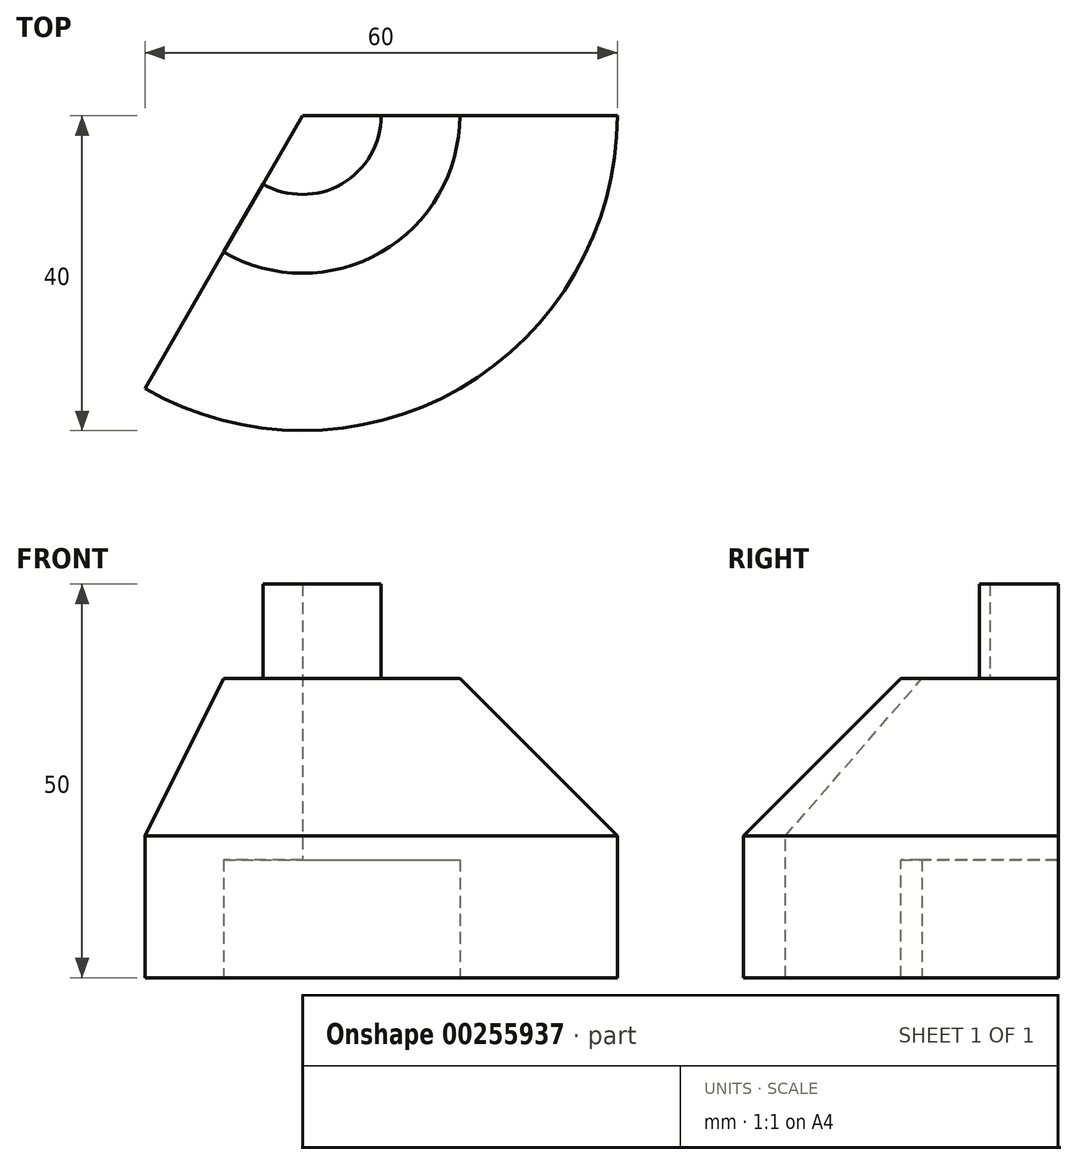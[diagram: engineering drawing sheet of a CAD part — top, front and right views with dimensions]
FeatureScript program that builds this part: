
annotation { "Feature Type Name" : "Feature", "Feature Type Description" : "" }
export const myFeature = defineFeature(function(context is Context, id is Id, definition is map)
    precondition{}
    {
        {
            var Q0;
            Q0=qCreatedBy(makeId("Front.planeOp"),FACE);
            var sketch = newSketch(context, id + "F0", { "sketchPlane" : qUnion([Q0])});
            skLineSegment(sketch, "E0", {"start": v(15.92, 20.7) * mm, "end": v(15.92, -14.3) * mm});
            skLineSegment(sketch, "E1", {"start": v(15.92, -14.3) * mm, "end": v(35.92, -14.3) * mm});
            skLineSegment(sketch, "E2", {"start": v(35.92, -14.3) * mm, "end": v(35.92, -29.3) * mm});
            skLineSegment(sketch, "E3", {"start": v(35.92, -29.3) * mm, "end": v(55.92, -29.3) * mm});
            skLineSegment(sketch, "E4", {"start": v(55.92, -29.3) * mm, "end": v(55.92, -11.3) * mm});
            skLineSegment(sketch, "E5", {"start": v(55.92, -11.3) * mm, "end": v(35.92, 8.7) * mm});
            skLineSegment(sketch, "E6", {"start": v(25.92, 8.7) * mm, "end": v(35.92, 8.7) * mm});
            skLineSegment(sketch, "E7", {"start": v(15.92, 20.7) * mm, "end": v(25.92, 20.7) * mm});
            skLineSegment(sketch, "E8", {"start": v(25.92, 20.7) * mm, "end": v(25.92, 8.7) * mm});
            skSolve(sketch);
        }
        {
            var Q0;
            Q0=makeQuery(id+"F0.imprint","IMPRINT",FACE,{"disambiguationData":[TD([[makeQuery(id+"F0.imprint","IMPRINT",EDGE,{"derivedFrom":sQuery(id+"F0.wireOp",EDGE,"E0")}),1.0]])]});
            var Q1;
            Q1=sQuery(id+"F0.wireOp",EDGE,"E0");
            revolve(context, id + "F1", {"entities" : qUnion([Q0]), "axis" : qUnion([Q1]), "revolveType" : RevolveType.ONE_DIRECTION, "angle" : 120 * degree});
        }
    });
